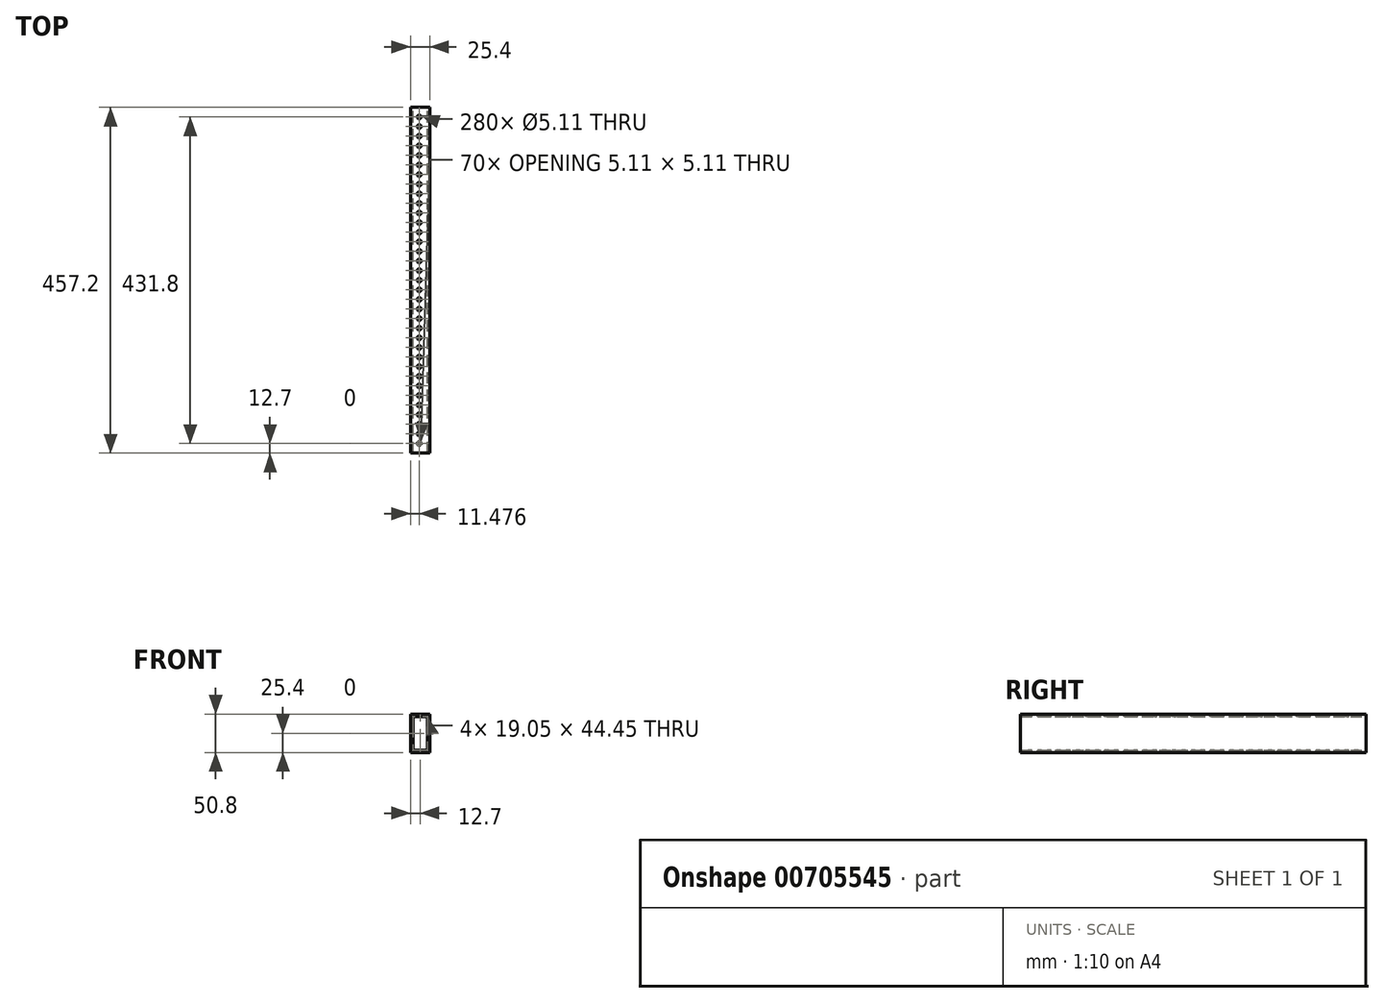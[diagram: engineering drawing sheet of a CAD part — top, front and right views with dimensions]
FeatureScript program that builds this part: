
annotation { "Feature Type Name" : "Feature", "Feature Type Description" : "" }
export const myFeature = defineFeature(function(context is Context, id is Id, definition is map)
    precondition{}
    {
        {
            var Q0;
            Q0=qCreatedBy(makeId("Front.planeOp"),FACE);
            var sketch = newSketch(context, id + "F0", { "sketchPlane" : qUnion([Q0])});
            skLineSegment(sketch, "E0.bottom", {"start": v(12.7, -25.4) * mm, "end": v(-12.7, -25.4) * mm});
            skLineSegment(sketch, "E0.top", {"start": v(12.7, 25.4) * mm, "end": v(-12.7, 25.4) * mm});
            skLineSegment(sketch, "E0.left", {"start": v(12.7, -25.4) * mm, "end": v(12.7, 25.4) * mm});
            skLineSegment(sketch, "E0.right", {"start": v(-12.7, -25.4) * mm, "end": v(-12.7, 25.4) * mm});
            skPoint(sketch, "E0.middle", {"position": v(0, 0) * mm});
            skLineSegment(sketch, "E1.0", {"start": v(9.53, 22.22) * mm, "end": v(-9.53, 22.22) * mm});
            skLineSegment(sketch, "E1.1", {"start": v(9.53, -22.23) * mm, "end": v(9.53, 22.22) * mm});
            skLineSegment(sketch, "E1.2", {"start": v(9.53, -22.23) * mm, "end": v(-9.53, -22.23) * mm});
            skLineSegment(sketch, "E1.3", {"start": v(-9.53, -22.23) * mm, "end": v(-9.53, 22.22) * mm});
            skSolve(sketch);
        }
        {
            var Q0;
            Q0=makeQuery(id+"F0.imprint","IMPRINT",FACE,{"disambiguationData":[TD([[makeQuery(id+"F0.imprint","IMPRINT",EDGE,{"derivedFrom":sQuery(id+"F0.wireOp",EDGE,"E0.bottom")}),-1.0]])]});
            extrude(context, id + "F1", {"entities" : qUnion([Q0]), "endBound" : BoundingType.SYMMETRIC, "depth" : 457.2 * mm, "offsetDistance" : 25.4 * mm});
        }
        {
            var Q0;
            Q0=makeQuery(id+"F1.opExtrude","SWEPT_FACE",FACE,{"disambiguationData":[OSD([sQuery(id+"F0.wireOp",EDGE,"E0.top")])]});
            var sketch = newSketch(context, id + "F2", { "sketchPlane" : qUnion([Q0])});
            skCircle(sketch, "E2", {"center": v(-1.22, -215.9) * mm, "radius": 2.55 * mm});
            skCircle(sketch, "E3.0.1.0", {"center": v(-1.22, -203.2) * mm, "radius": 2.55 * mm});
            skCircle(sketch, "E3.0.2.0", {"center": v(-1.22, -190.5) * mm, "radius": 2.55 * mm});
            skCircle(sketch, "E3.0.3.0", {"center": v(-1.22, -177.8) * mm, "radius": 2.55 * mm});
            skCircle(sketch, "E3.0.4.0", {"center": v(-1.22, -165.1) * mm, "radius": 2.55 * mm});
            skCircle(sketch, "E3.0.5.0", {"center": v(-1.22, -152.4) * mm, "radius": 2.55 * mm});
            skCircle(sketch, "E3.0.6.0", {"center": v(-1.22, -139.7) * mm, "radius": 2.55 * mm});
            skCircle(sketch, "E3.0.7.0", {"center": v(-1.22, -127) * mm, "radius": 2.55 * mm});
            skCircle(sketch, "E3.0.8.0", {"center": v(-1.22, -114.3) * mm, "radius": 2.55 * mm});
            skCircle(sketch, "E3.0.9.0", {"center": v(-1.22, -101.6) * mm, "radius": 2.55 * mm});
            skCircle(sketch, "E3.0.10.0", {"center": v(-1.22, -88.9) * mm, "radius": 2.55 * mm});
            skCircle(sketch, "E3.0.11.0", {"center": v(-1.22, -76.2) * mm, "radius": 2.55 * mm});
            skCircle(sketch, "E3.0.12.0", {"center": v(-1.22, -63.5) * mm, "radius": 2.55 * mm});
            skCircle(sketch, "E3.0.13.0", {"center": v(-1.22, -50.8) * mm, "radius": 2.55 * mm});
            skCircle(sketch, "E3.0.14.0", {"center": v(-1.22, -38.1) * mm, "radius": 2.55 * mm});
            skCircle(sketch, "E3.0.15.0", {"center": v(-1.22, -25.4) * mm, "radius": 2.55 * mm});
            skLineSegment(sketch, "E3.direction1", {"start": v(-1.22, -215.9) * mm, "end": v(24.18, -215.9) * mm, "construction": true});
            skLineSegment(sketch, "E3.direction2", {"start": v(-1.22, -215.9) * mm, "end": v(-1.22, -203.2) * mm, "construction": true});
            skCircle(sketch, "E4.0.0.16", {"center": v(-1.22, -12.7) * mm, "radius": 2.55 * mm});
            skCircle(sketch, "E4.0.0.17", {"center": v(-1.22, 0) * mm, "radius": 2.55 * mm});
            skCircle(sketch, "E4.0.0.18", {"center": v(-1.22, 12.7) * mm, "radius": 2.55 * mm});
            skCircle(sketch, "E4.0.0.19", {"center": v(-1.22, 25.4) * mm, "radius": 2.55 * mm});
            skCircle(sketch, "E4.0.0.20", {"center": v(-1.22, 38.1) * mm, "radius": 2.55 * mm});
            skCircle(sketch, "E4.0.0.21", {"center": v(-1.22, 50.8) * mm, "radius": 2.55 * mm});
            skCircle(sketch, "E4.0.0.22", {"center": v(-1.22, 63.5) * mm, "radius": 2.55 * mm});
            skCircle(sketch, "E4.0.0.23", {"center": v(-1.22, 76.2) * mm, "radius": 2.55 * mm});
            skCircle(sketch, "E5.0.0.24", {"center": v(-1.22, 88.9) * mm, "radius": 2.55 * mm});
            skCircle(sketch, "E5.0.0.25", {"center": v(-1.22, 101.6) * mm, "radius": 2.55 * mm});
            skCircle(sketch, "E5.0.0.26", {"center": v(-1.22, 114.3) * mm, "radius": 2.55 * mm});
            skCircle(sketch, "E5.0.0.27", {"center": v(-1.22, 127) * mm, "radius": 2.55 * mm});
            skCircle(sketch, "E5.0.0.28", {"center": v(-1.22, 139.7) * mm, "radius": 2.55 * mm});
            skCircle(sketch, "E5.0.0.29", {"center": v(-1.22, 152.4) * mm, "radius": 2.55 * mm});
            skCircle(sketch, "E5.0.0.30", {"center": v(-1.22, 165.1) * mm, "radius": 2.55 * mm});
            skCircle(sketch, "E5.0.0.31", {"center": v(-1.22, 177.8) * mm, "radius": 2.55 * mm});
            skCircle(sketch, "E5.0.0.32", {"center": v(-1.22, 190.5) * mm, "radius": 2.55 * mm});
            skCircle(sketch, "E5.0.0.33", {"center": v(-1.22, 203.2) * mm, "radius": 2.55 * mm});
            skCircle(sketch, "E5.0.0.34", {"center": v(-1.22, 215.9) * mm, "radius": 2.55 * mm});
            skSolve(sketch);
        }
        {
            var Q0;
            Q0=makeQuery(id+"F2.imprint","IMPRINT",FACE,{"disambiguationData":[TD([[makeQuery(id+"F2.imprint","IMPRINT",EDGE,{"derivedFrom":sQuery(id+"F2.wireOp",EDGE,"E2")}),-1.0]])]});
            extrude(context, id + "F3", {"entities" : qUnion([Q0]), "operationType" : NewBodyOperationType.INTERSECT, "endBound" : BoundingType.THROUGH_ALL, "oppositeDirection" : true, "depth" : 25.4 * mm, "offsetDistance" : 25.4 * mm});
        }
    });
